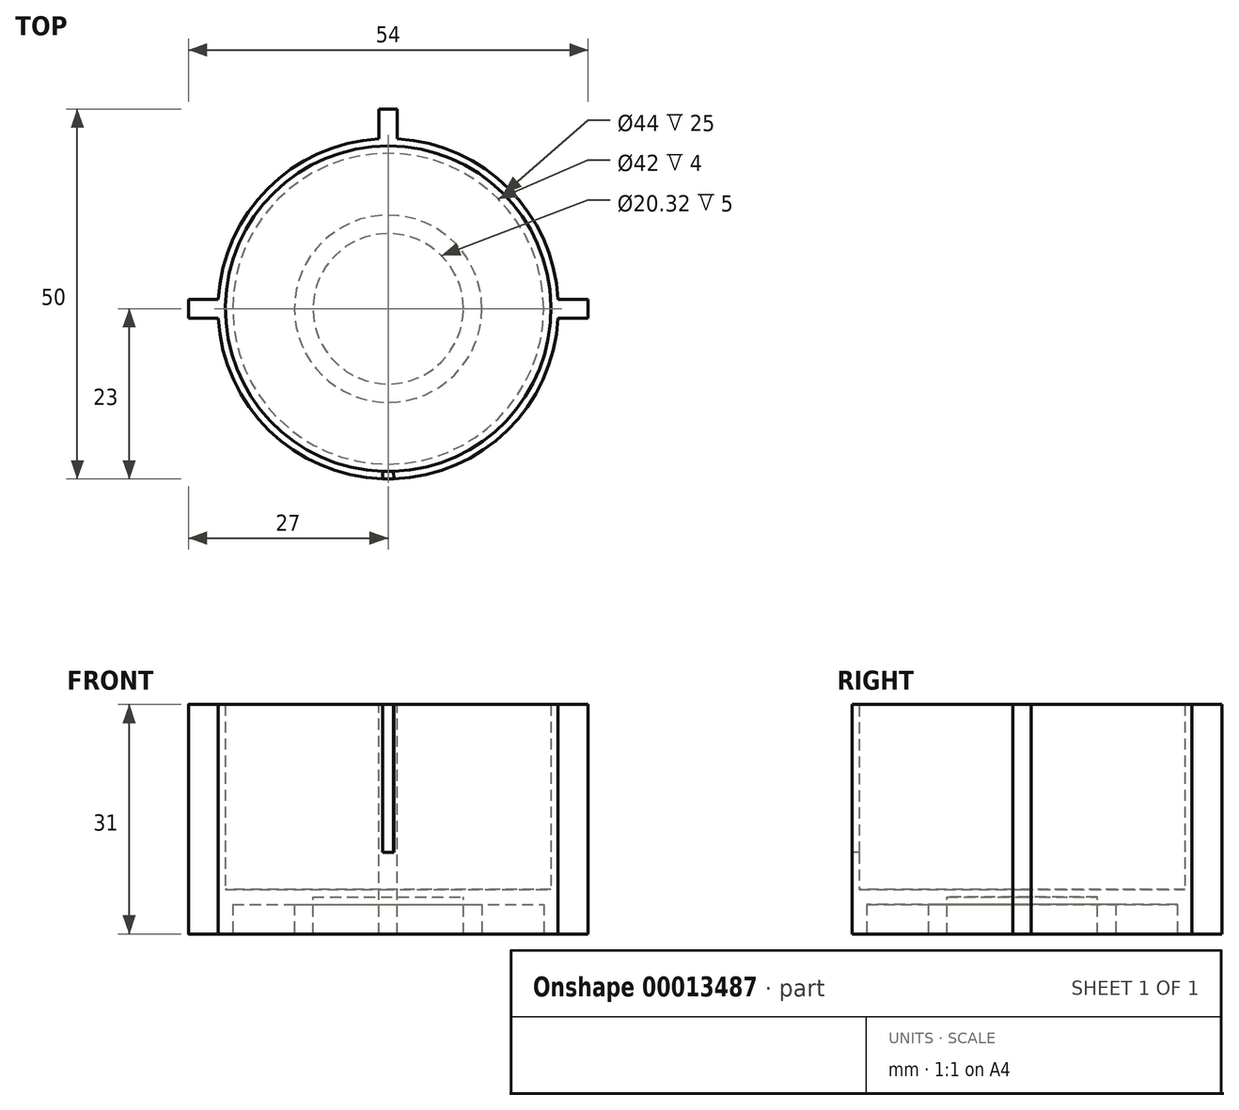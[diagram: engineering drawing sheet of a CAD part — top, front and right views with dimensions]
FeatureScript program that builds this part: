
annotation { "Feature Type Name" : "Feature", "Feature Type Description" : "" }
export const myFeature = defineFeature(function(context is Context, id is Id, definition is map)
    precondition{}
    {
        {
            var Q0;
            Q0=qCreatedBy(makeId("Top.planeOp"),FACE);
            var sketch = newSketch(context, id + "F0", { "sketchPlane" : qUnion([Q0])});
            skCircle(sketch, "E0", {"center": v(0, 0) * mm, "radius": 22 * mm});
            skCircle(sketch, "E1", {"center": v(0, 0) * mm, "radius": 23 * mm});
            skSolve(sketch);
        }
        {
            var Q0;
            Q0 = qSketchRegion(id + "F0", true);
            extrude(context, id + "F1", {"entities" : qUnion([Q0]), "depth" : 25 * mm});
        }
        {
            var Q0;
            Q0=makeQuery(id+"F1.opExtrude","CAP_FACE",FACE,{"disambiguationData":[OSD([sQuery(id+"F0.wireOp",EDGE,"E0"),sQuery(id+"F0.wireOp",EDGE,"E1")])],"isStart":true});
            var sketch = newSketch(context, id + "F2", { "sketchPlane" : qUnion([Q0])});
            skCircle(sketch, "E2", {"center": v(0, 0) * mm, "radius": 23 * mm});
            skSolve(sketch);
        }
        {
            var Q0;
            Q0 = qSketchRegion(id + "F2", true);
            extrude(context, id + "F3", {"entities" : qUnion([Q0]), "operationType" : NewBodyOperationType.ADD, "depth" : 1 * mm});
        }
        {
            var Q0;
            Q0=makeQuery(id+"F3.opExtrude","CAP_FACE",FACE,{"disambiguationData":[OSD([sQuery(id+"F2.wireOp",EDGE,"E2")])],"isStart":false});
            var sketch = newSketch(context, id + "F4", { "sketchPlane" : qUnion([Q0])});
            skCircle(sketch, "E3", {"center": v(0, 0) * mm, "radius": 23 * mm});
            skCircle(sketch, "E4", {"center": v(0, 0) * mm, "radius": 10.16 * mm});
            skSolve(sketch);
        }
        {
            var Q0;
            Q0 = qSketchRegion(id + "F4", true);
            extrude(context, id + "F5", {"entities" : qUnion([Q0]), "operationType" : NewBodyOperationType.ADD, "depth" : 5 * mm});
        }
        {
            var Q0;
            Q0=makeQuery(id+"F5.opExtrude","CAP_FACE",FACE,{"disambiguationData":[OSD([sQuery(id+"F4.wireOp",EDGE,"E3"),sQuery(id+"F4.wireOp",EDGE,"E4")])],"isStart":false});
            var sketch = newSketch(context, id + "F6", { "sketchPlane" : qUnion([Q0])});
            skCircle(sketch, "E5", {"center": v(0, 0) * mm, "radius": 12.66 * mm});
            skCircle(sketch, "E6", {"center": v(0, 0) * mm, "radius": 21 * mm});
            skSolve(sketch);
        }
        {
            var Q0;
            Q0 = qSketchRegion(id + "F6", true);
            extrude(context, id + "F7", {"entities" : qUnion([Q0]), "operationType" : NewBodyOperationType.REMOVE, "oppositeDirection" : true, "depth" : 4 * mm});
        }
        {
            var Q0;
            Q0=makeQuery(id+"F1.opExtrude","CAP_FACE",FACE,{"disambiguationData":[OSD([sQuery(id+"F0.wireOp",EDGE,"E0"),sQuery(id+"F0.wireOp",EDGE,"E1")])],"isStart":false});
            var sketch = newSketch(context, id + "F8", { "sketchPlane" : qUnion([Q0])});
            skArc(sketch, "E7", {"start": v(-0.72, -21.99) * mm, "mid": v(0, -22) * mm, "end": v(0.72, -21.99) * mm});
            skLineSegment(sketch, "E8", {"start": v(0.72, -21.99) * mm, "end": v(0.75, -22.99) * mm});
            skLineSegment(sketch, "E9", {"start": v(-0.72, -21.99) * mm, "end": v(-0.75, -22.99) * mm});
            skPoint(sketch, "E10", {"position": v(0, -23) * mm});
            skArc(sketch, "E11", {"start": v(-0.75, -22.99) * mm, "mid": v(0, -23) * mm, "end": v(0.75, -22.99) * mm});
            skSolve(sketch);
        }
        {
            var Q0;
            Q0 = qSketchRegion(id + "F8", true);
            extrude(context, id + "F9", {"entities" : qUnion([Q0]), "operationType" : NewBodyOperationType.REMOVE, "oppositeDirection" : true, "depth" : 20 * mm});
        }
        {
            var Q0;
            Q0=makeQuery(id+"F1.opExtrude","CAP_FACE",FACE,{"disambiguationData":[OSD([sQuery(id+"F0.wireOp",EDGE,"E0"),sQuery(id+"F0.wireOp",EDGE,"E1")])],"isStart":false});
            var sketch = newSketch(context, id + "F10", { "sketchPlane" : qUnion([Q0])});
            skArc(sketch, "E12", {"start": v(-22.97, 1.25) * mm, "mid": v(-23, 0) * mm, "end": v(-22.97, -1.25) * mm});
            skArc(sketch, "E13", {"start": v(-26.97, 1.25) * mm, "mid": v(-27, 0) * mm, "end": v(-26.97, -1.25) * mm});
            skLineSegment(sketch, "E14.rect.bottom", {"start": v(-26.97, 1.25) * mm, "end": v(-22.97, 1.25) * mm});
            skLineSegment(sketch, "E14.rect.top", {"start": v(-26.97, -1.25) * mm, "end": v(-22.97, -1.25) * mm});
            skLineSegment(sketch, "E14.rect.left", {"start": v(-26.97, 1.25) * mm, "end": v(-26.97, -1.25) * mm});
            skLineSegment(sketch, "E14.rect.right", {"start": v(26.97, 1.25) * mm, "end": v(26.97, -1.25) * mm});
            skLineSegment(sketch, "E15.rect.bottom", {"start": v(-1.25, 26.97) * mm, "end": v(1.25, 26.97) * mm});
            skLineSegment(sketch, "E15.rect.left", {"start": v(-1.25, 26.97) * mm, "end": v(-1.25, 22.97) * mm});
            skLineSegment(sketch, "E15.rect.right", {"start": v(1.25, 26.97) * mm, "end": v(1.25, 22.97) * mm});
            skArc(sketch, "E16.trimOffspring", {"start": v(1.25, 26.97) * mm, "mid": v(0, 27) * mm, "end": v(-1.25, 26.97) * mm});
            skArc(sketch, "E17.trimOffspring", {"start": v(1.25, 22.97) * mm, "mid": v(0, 23) * mm, "end": v(-1.25, 22.97) * mm});
            skLineSegment(sketch, "E18.trimOffspring", {"start": v(22.97, 1.25) * mm, "end": v(26.97, 1.25) * mm});
            skLineSegment(sketch, "E19.trimOffspring", {"start": v(22.97, -1.25) * mm, "end": v(26.97, -1.25) * mm});
            skArc(sketch, "E20.trimOffspring", {"start": v(26.97, -1.25) * mm, "mid": v(27, 0) * mm, "end": v(26.97, 1.25) * mm});
            skArc(sketch, "E21.trimOffspring", {"start": v(22.97, -1.25) * mm, "mid": v(23, 0) * mm, "end": v(22.97, 1.25) * mm});
            skSolve(sketch);
        }
        {
            var Q0;
            Q0 = qSketchRegion(id + "F10", true);
            var Q1;
            {var subQ0=sQuery(id+"F4.wireOp",EDGE,"E3");Q1=makeQuery(id+"F7.boolean.opBoolean","SPLIT",FACE,{"disambiguationData":[TD([makeQuery(id+"F1.opExtrude","SWEPT_FACE",FACE,{"disambiguationData":[OSD([sQuery(id+"F0.wireOp",EDGE,"E1")])]})])],"derivedFrom":makeQuery(id+"F5.opExtrude","CAP_FACE",FACE,{"disambiguationData":[OSD([subQ0,sQuery(id+"F4.wireOp",EDGE,"E4")])],"isStart":false})});}
            extrude(context, id + "F11", {"entities" : qUnion([Q0]), "operationType" : NewBodyOperationType.ADD, "endBound" : BoundingType.UP_TO_SURFACE, "oppositeDirection" : true, "endBoundEntityFace" : qUnion([Q1]), "depth" : 25 * mm});
        }
    });
